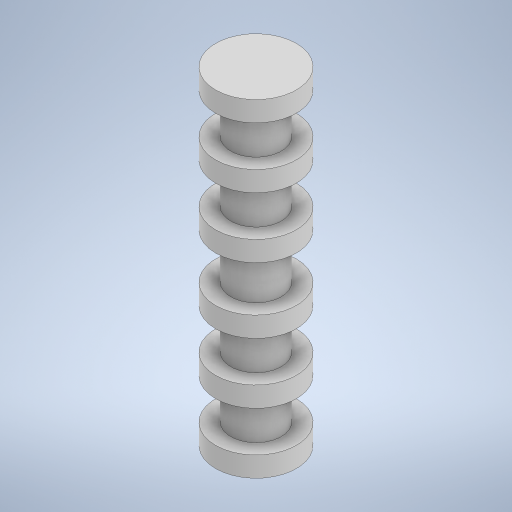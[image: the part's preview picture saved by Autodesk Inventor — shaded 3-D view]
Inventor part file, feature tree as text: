
AUTODESK INVENTOR PART (.ipt)
format: ipt  version: 2023 (Build 270158000, 158)  size: 295,424 bytes
history: native  units: in
note: dims shown in document units (in); Inventor stores cm internally (conversion verified against a paired STEP export)
features: revolve x1, sketch x1
ambient origin geometry x8: Origin, YZ Plane, XZ Plane, XY Plane, X Axis, Y Axis, Z Axis, Center Point
bodies: Solid1 (feature_tree)
feature tree (2):
  revolve  "Revolution1"  [1 undecoded]
  sketch  "Sketch1"  dims[d1=0.157in d2=0.093in d3=0.125in d5=0.125in d7=0.125in d9=90.0deg]
note: 1 required parameter value undecoded (feature->parameter linkage not recoverable at this tier; creation-order binding heuristic only, values carry confidence <= 0.55)
